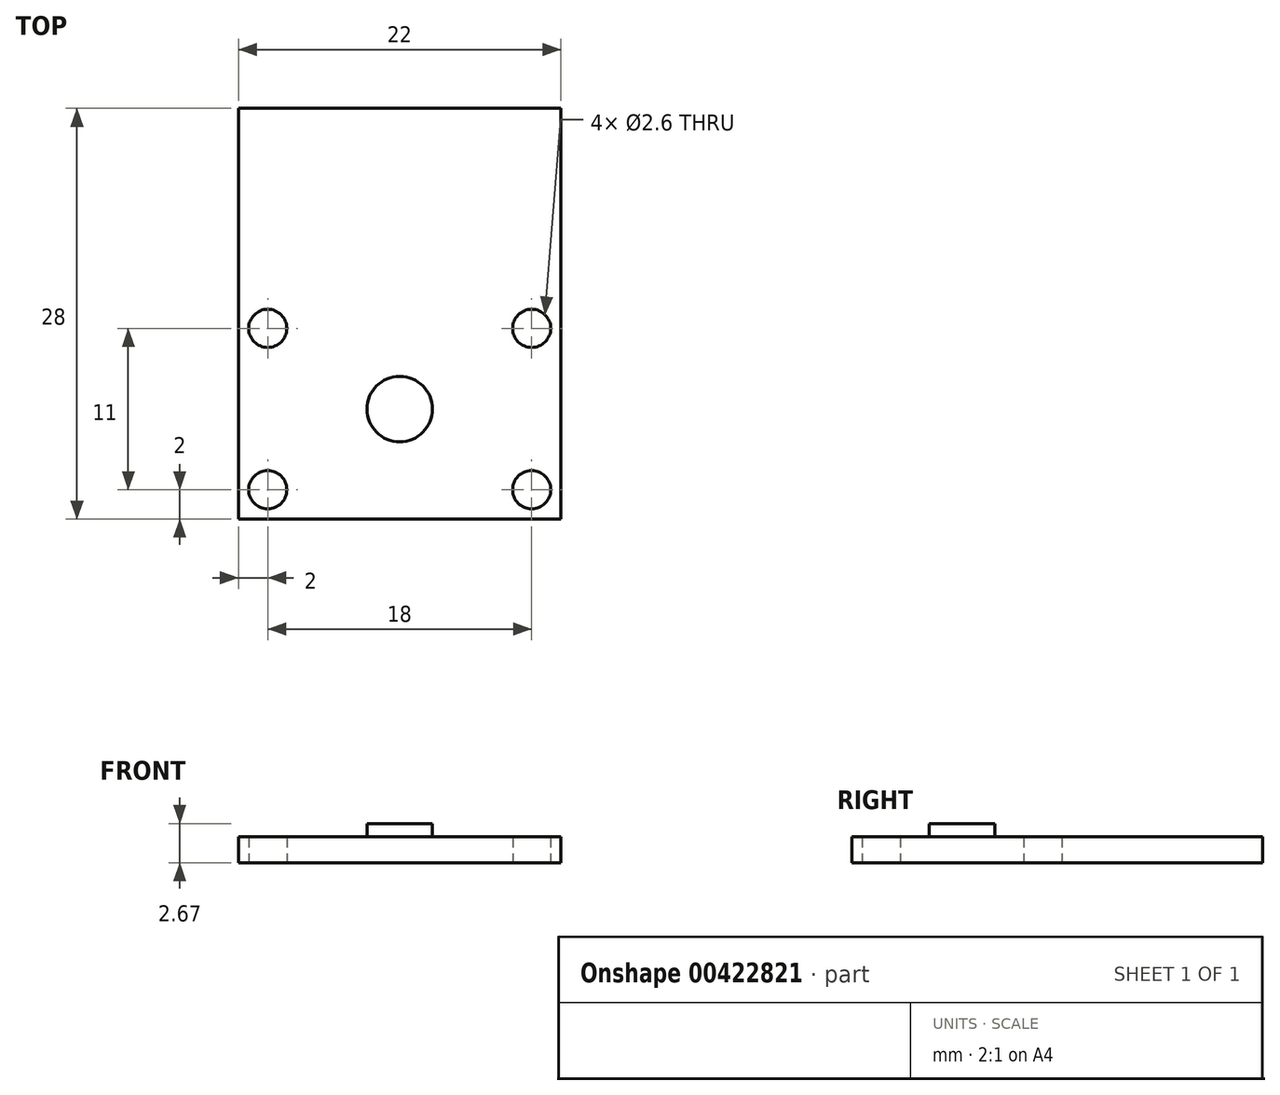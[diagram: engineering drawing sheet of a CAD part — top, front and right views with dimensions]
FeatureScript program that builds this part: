
annotation { "Feature Type Name" : "Feature", "Feature Type Description" : "" }
export const myFeature = defineFeature(function(context is Context, id is Id, definition is map)
    precondition{}
    {
        {
            var Q0;
            Q0=qCreatedBy(makeId("Top.planeOp"),FACE);
            var sketch = newSketch(context, id + "F0", { "sketchPlane" : qUnion([Q0])});
            skLineSegment(sketch, "E0.bottom", {"start": v(-11, 20.5) * mm, "end": v(11, 20.5) * mm});
            skLineSegment(sketch, "E0.top", {"start": v(-11, -7.5) * mm, "end": v(11, -7.5) * mm});
            skLineSegment(sketch, "E0.left", {"start": v(-11, 20.5) * mm, "end": v(-11, -7.5) * mm});
            skLineSegment(sketch, "E0.right", {"start": v(11, 20.5) * mm, "end": v(11, -7.5) * mm});
            skCircle(sketch, "E1", {"center": v(-9, -5.5) * mm, "radius": 1.3 * mm});
            skLineSegment(sketch, "E2", {"start": v(0, 0) * mm, "end": v(-16.7, 0) * mm, "construction": true});
            skLineSegment(sketch, "E3", {"start": v(0, 0) * mm, "end": v(0, -8.66) * mm, "construction": true});
            skPoint(sketch, "E3.endSnap0", {"position": v(0, -7.5) * mm});
            skCircle(sketch, "E4.MirrorC", {"center": v(9, -5.5) * mm, "radius": 1.3 * mm});
            skCircle(sketch, "E5.MirrorC", {"center": v(9, 5.5) * mm, "radius": 1.3 * mm});
            skCircle(sketch, "E6.MirrorC", {"center": v(-9, 5.5) * mm, "radius": 1.3 * mm});
            skPoint(sketch, "E7", {"position": v(0, 0) * mm});
            skSolve(sketch);
        }
        {
            var Q0;
            Q0 = qSketchRegion(id + "F0", true);
            extrude(context, id + "F1", {"entities" : qUnion([Q0]), "depth" : 1.78 * mm});
        }
        {
            var Q0;
            Q0=makeQuery(id+"F1.opExtrude","CAP_FACE",FACE,{"disambiguationData":[OSD([sQuery(id+"F0.wireOp",EDGE,"E0.bottom"),sQuery(id+"F0.wireOp",EDGE,"E0.top"),sQuery(id+"F0.wireOp",EDGE,"E0.left"),sQuery(id+"F0.wireOp",EDGE,"E0.right"),sQuery(id+"F0.wireOp",EDGE,"E1"),sQuery(id+"F0.wireOp",EDGE,"E4.MirrorC"),sQuery(id+"F0.wireOp",EDGE,"E5.MirrorC"),sQuery(id+"F0.wireOp",EDGE,"E6.MirrorC")])],"isStart":false});
            var sketch = newSketch(context, id + "F2", { "sketchPlane" : qUnion([Q0])});
            skCircle(sketch, "E8", {"center": v(0, 0) * mm, "radius": 2.23 * mm});
            skSolve(sketch);
        }
        {
            var Q0;
            Q0 = qSketchRegion(id + "F2", true);
            extrude(context, id + "F3", {"entities" : qUnion([Q0]), "operationType" : NewBodyOperationType.ADD, "depth" : 0.89 * mm});
        }
    });
